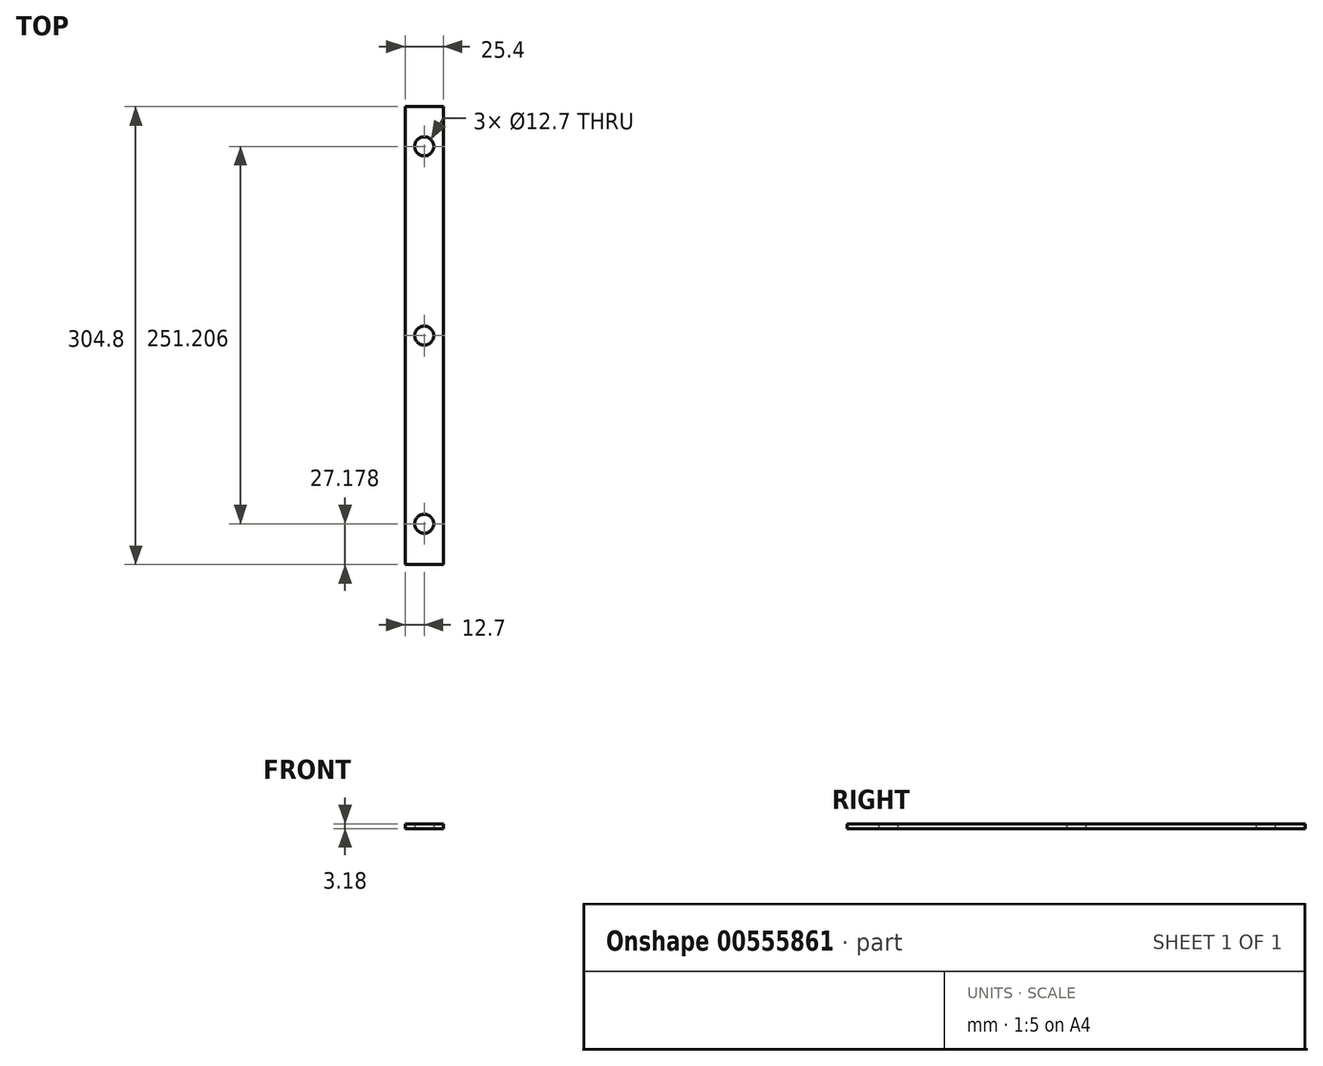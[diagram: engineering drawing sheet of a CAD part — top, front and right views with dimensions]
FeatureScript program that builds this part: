
annotation { "Feature Type Name" : "Feature", "Feature Type Description" : "" }
export const myFeature = defineFeature(function(context is Context, id is Id, definition is map)
    precondition{}
    {
        {
            var Q0;
            Q0=qCreatedBy(makeId("Top.planeOp"),FACE);
            var sketch = newSketch(context, id + "F0", { "sketchPlane" : qUnion([Q0])});
            skLineSegment(sketch, "E0.bottom", {"start": v(-12.7, -152.4) * mm, "end": v(12.7, -152.4) * mm});
            skLineSegment(sketch, "E0.top", {"start": v(-12.7, 152.4) * mm, "end": v(12.7, 152.4) * mm});
            skLineSegment(sketch, "E0.left", {"start": v(-12.7, -152.4) * mm, "end": v(-12.7, 152.4) * mm});
            skLineSegment(sketch, "E0.right", {"start": v(12.7, -152.4) * mm, "end": v(12.7, 152.4) * mm});
            skPoint(sketch, "E0.middle", {"position": v(0, 0) * mm});
            skSolve(sketch);
        }
        {
            var Q0;
            Q0=makeQuery(id+"F0.imprint","IMPRINT",FACE,{"disambiguationData":[TD([[makeQuery(id+"F0.imprint","IMPRINT",EDGE,{"derivedFrom":sQuery(id+"F0.wireOp",EDGE,"E0.bottom")}),1.0]])]});
            extrude(context, id + "F1", {"entities" : qUnion([Q0]), "depth" : 3.17 * mm, "offsetDistance" : 25.4 * mm});
        }
        {
            var Q0;
            Q0=qCreatedBy(makeId("Top.planeOp"),FACE);
            var sketch = newSketch(context, id + "F2", { "sketchPlane" : qUnion([Q0])});
            skCircle(sketch, "E1", {"center": v(0, 0) * mm, "radius": 6.88 * mm});
            skCircle(sketch, "E2.0.1.0", {"center": v(0, -125.22) * mm, "radius": 6.88 * mm});
            skCircle(sketch, "E3.0.1.0", {"center": v(0, 125.98) * mm, "radius": 6.88 * mm});
            skSolve(sketch);
        }
        {
            var Q0;
            Q0=sQuery(id+"F2.wireOp",VERTEX,"E1.center");
            var Q1;
            Q1=sQuery(id+"F2.wireOp",VERTEX,"E2.0.1.0.center");
            var Q2;
            Q2=sQuery(id+"F2.wireOp",VERTEX,"E3.0.1.0.center");
            var Q3;
            Q3=makeQuery(id+"F1.opExtrude","SWEPT_BODY",BODY,{"disambiguationData":[OSD([sQuery(id+"F0.wireOp",EDGE,"E0.bottom"),sQuery(id+"F0.wireOp",EDGE,"E0.top"),sQuery(id+"F0.wireOp",EDGE,"E0.left"),sQuery(id+"F0.wireOp",EDGE,"E0.right")])]});
            hole(context, id + "F3", {"style" : HoleStyle.SIMPLE, "endStyle" : HoleEndStyle.BLIND, "oppositeDirection" : true, "holeDiameter" : 12.7 * mm, "holeDepth" : 25.4 * mm, "isTappedThrough" : true, "tappedDepth" : 12.7 * mm, "tapClearance" : 3, "startFromSketch" : true, "locations" : qUnion([Q0, Q1, Q2]), "scope" : qUnion([Q3])});
        }
    });
